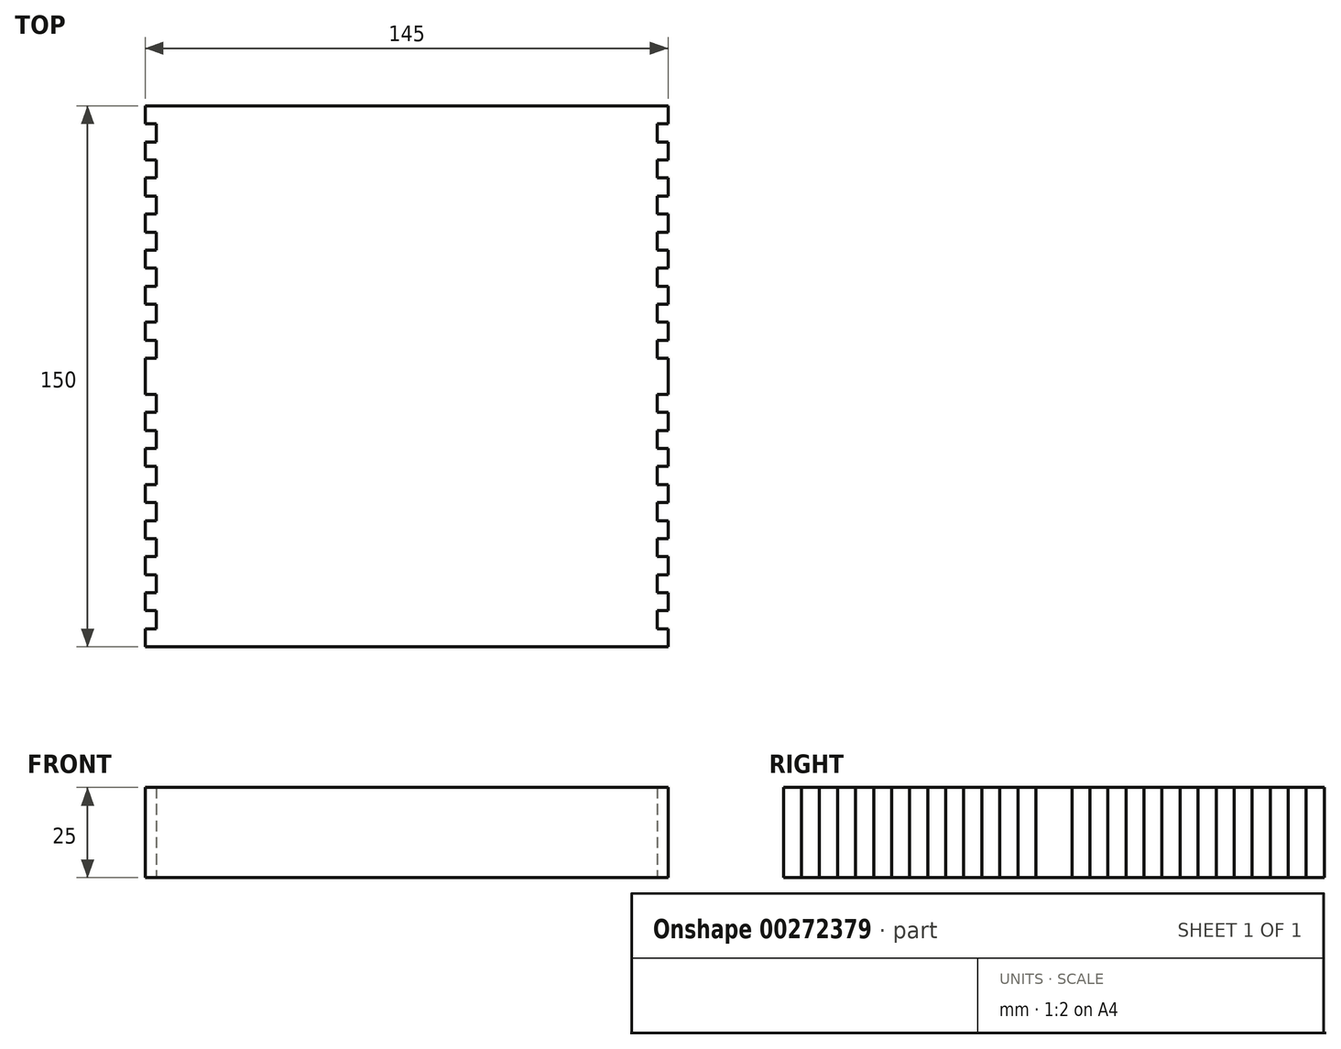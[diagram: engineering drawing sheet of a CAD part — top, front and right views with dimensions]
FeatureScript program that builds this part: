
annotation { "Feature Type Name" : "Feature", "Feature Type Description" : "" }
export const myFeature = defineFeature(function(context is Context, id is Id, definition is map)
    precondition{}
    {
        {
            var Q0;
            Q0=qCreatedBy(makeId("Top.planeOp"),FACE);
            var sketch = newSketch(context, id + "F0", { "sketchPlane" : qUnion([Q0])});
            skLineSegment(sketch, "E0.bottom", {"start": v(72.5, 75) * mm, "end": v(-72.5, 75) * mm});
            skLineSegment(sketch, "E0.top", {"start": v(72.5, -75) * mm, "end": v(-72.5, -75) * mm});
            skPoint(sketch, "E0.middle", {"position": v(0, 0) * mm});
            skLineSegment(sketch, "E1", {"start": v(-72.5, 0) * mm, "end": v(72.5, 0) * mm, "construction": true});
            skLineSegment(sketch, "E2", {"start": v(0, 75) * mm, "end": v(0, -75) * mm, "construction": true});
            skLineSegment(sketch, "E3", {"start": v(-72.5, 75) * mm, "end": v(-72.5, 70) * mm});
            skLineSegment(sketch, "E4", {"start": v(-72.5, 70) * mm, "end": v(-69.5, 70) * mm});
            skLineSegment(sketch, "E5", {"start": v(-69.5, 70) * mm, "end": v(-69.5, 65) * mm});
            skLineSegment(sketch, "E6", {"start": v(-69.5, 65) * mm, "end": v(-72.5, 65) * mm});
            skLineSegment(sketch, "E7", {"start": v(-72.5, 65) * mm, "end": v(-72.5, 60) * mm});
            skLineSegment(sketch, "E8", {"start": v(-72.5, 60) * mm, "end": v(-69.5, 60) * mm});
            skLineSegment(sketch, "E9", {"start": v(-69.5, 60) * mm, "end": v(-69.5, 55) * mm});
            skLineSegment(sketch, "E10", {"start": v(-69.5, 55) * mm, "end": v(-72.5, 55) * mm});
            skLineSegment(sketch, "E11", {"start": v(-72.5, 55) * mm, "end": v(-72.5, 50) * mm});
            skLineSegment(sketch, "E12", {"start": v(-72.5, 50) * mm, "end": v(-69.5, 50) * mm});
            skLineSegment(sketch, "E13", {"start": v(-69.5, 50) * mm, "end": v(-69.5, 45) * mm});
            skLineSegment(sketch, "E14", {"start": v(-69.5, 45) * mm, "end": v(-72.5, 45) * mm});
            skLineSegment(sketch, "E15", {"start": v(-72.5, 45) * mm, "end": v(-72.5, 40) * mm});
            skLineSegment(sketch, "E16", {"start": v(-72.5, 40) * mm, "end": v(-69.5, 40) * mm});
            skLineSegment(sketch, "E17", {"start": v(-69.5, 40) * mm, "end": v(-69.5, 35) * mm});
            skLineSegment(sketch, "E18", {"start": v(-69.5, 35) * mm, "end": v(-72.5, 35) * mm});
            skLineSegment(sketch, "E19", {"start": v(-72.5, 35) * mm, "end": v(-72.5, 30) * mm});
            skLineSegment(sketch, "E20", {"start": v(-72.5, 30) * mm, "end": v(-69.5, 30) * mm});
            skLineSegment(sketch, "E21", {"start": v(-69.5, 30) * mm, "end": v(-69.5, 25) * mm});
            skLineSegment(sketch, "E22", {"start": v(-69.5, 25) * mm, "end": v(-72.5, 25) * mm});
            skLineSegment(sketch, "E23", {"start": v(-72.5, 25) * mm, "end": v(-72.5, 20) * mm});
            skLineSegment(sketch, "E24", {"start": v(-72.5, 20) * mm, "end": v(-69.5, 20) * mm});
            skLineSegment(sketch, "E25", {"start": v(-69.5, 20) * mm, "end": v(-69.5, 15) * mm});
            skLineSegment(sketch, "E26", {"start": v(-69.5, 15) * mm, "end": v(-72.5, 15) * mm});
            skLineSegment(sketch, "E27", {"start": v(-72.5, 15) * mm, "end": v(-72.5, 10) * mm});
            skLineSegment(sketch, "E28", {"start": v(-72.5, 10) * mm, "end": v(-69.5, 10) * mm});
            skLineSegment(sketch, "E29", {"start": v(-69.5, 10) * mm, "end": v(-69.5, 5) * mm});
            skLineSegment(sketch, "E30", {"start": v(-69.5, 5) * mm, "end": v(-72.5, 5) * mm});
            skLineSegment(sketch, "E31", {"start": v(-72.5, 5) * mm, "end": v(-72.5, 0) * mm});
            skLineSegment(sketch, "E32.MirrorCS", {"start": v(-72.5, -75) * mm, "end": v(-72.5, -70) * mm});
            skLineSegment(sketch, "E33.MirrorCS", {"start": v(-69.5, -5) * mm, "end": v(-72.5, -5) * mm});
            skLineSegment(sketch, "E34.MirrorCS", {"start": v(-69.5, -45) * mm, "end": v(-72.5, -45) * mm});
            skLineSegment(sketch, "E35.MirrorCS", {"start": v(-72.5, -40) * mm, "end": v(-69.5, -40) * mm});
            skLineSegment(sketch, "E36.MirrorCS", {"start": v(-72.5, -15) * mm, "end": v(-72.5, -10) * mm});
            skLineSegment(sketch, "E37.MirrorCS", {"start": v(-72.5, -25) * mm, "end": v(-72.5, -20) * mm});
            skLineSegment(sketch, "E38.MirrorCS", {"start": v(-69.5, -55) * mm, "end": v(-72.5, -55) * mm});
            skLineSegment(sketch, "E39.MirrorCS", {"start": v(-69.5, -35) * mm, "end": v(-72.5, -35) * mm});
            skLineSegment(sketch, "E40.MirrorCS", {"start": v(-69.5, -60) * mm, "end": v(-69.5, -55) * mm});
            skLineSegment(sketch, "E41.MirrorCS", {"start": v(-72.5, -60) * mm, "end": v(-69.5, -60) * mm});
            skLineSegment(sketch, "E42.MirrorCS", {"start": v(-72.5, -5) * mm, "end": v(-72.5, 0) * mm});
            skLineSegment(sketch, "E43.MirrorCS", {"start": v(-72.5, -50) * mm, "end": v(-69.5, -50) * mm});
            skLineSegment(sketch, "E44.MirrorCS", {"start": v(-72.5, -30) * mm, "end": v(-69.5, -30) * mm});
            skLineSegment(sketch, "E45.MirrorCS", {"start": v(-72.5, -55) * mm, "end": v(-72.5, -50) * mm});
            skLineSegment(sketch, "E46.MirrorCS", {"start": v(-72.5, -45) * mm, "end": v(-72.5, -40) * mm});
            skLineSegment(sketch, "E47.MirrorCS", {"start": v(-69.5, -15) * mm, "end": v(-72.5, -15) * mm});
            skLineSegment(sketch, "E48.MirrorCS", {"start": v(-69.5, -65) * mm, "end": v(-72.5, -65) * mm});
            skLineSegment(sketch, "E49.MirrorCS", {"start": v(-69.5, -70) * mm, "end": v(-69.5, -65) * mm});
            skLineSegment(sketch, "E50.MirrorCS", {"start": v(-72.5, -10) * mm, "end": v(-69.5, -10) * mm});
            skLineSegment(sketch, "E51.MirrorCS", {"start": v(-72.5, -70) * mm, "end": v(-69.5, -70) * mm});
            skLineSegment(sketch, "E52.MirrorCS", {"start": v(-72.5, -20) * mm, "end": v(-69.5, -20) * mm});
            skLineSegment(sketch, "E53.MirrorCS", {"start": v(-72.5, -35) * mm, "end": v(-72.5, -30) * mm});
            skLineSegment(sketch, "E54.MirrorCS", {"start": v(-69.5, -25) * mm, "end": v(-72.5, -25) * mm});
            skLineSegment(sketch, "E55.MirrorCS", {"start": v(-69.5, -20) * mm, "end": v(-69.5, -15) * mm});
            skLineSegment(sketch, "E56.MirrorCS", {"start": v(-69.5, -50) * mm, "end": v(-69.5, -45) * mm});
            skLineSegment(sketch, "E57.MirrorCS", {"start": v(-69.5, -10) * mm, "end": v(-69.5, -5) * mm});
            skLineSegment(sketch, "E58.MirrorCS", {"start": v(-72.5, -65) * mm, "end": v(-72.5, -60) * mm});
            skLineSegment(sketch, "E59.MirrorCS", {"start": v(-69.5, -30) * mm, "end": v(-69.5, -25) * mm});
            skLineSegment(sketch, "E60.MirrorCS", {"start": v(-69.5, -40) * mm, "end": v(-69.5, -35) * mm});
            skLineSegment(sketch, "E61.MirrorCS", {"start": v(0, -75) * mm, "end": v(0, 75) * mm, "construction": true});
            skLineSegment(sketch, "E62.MirrorCS", {"start": v(72.5, 75) * mm, "end": v(72.5, 70) * mm});
            skLineSegment(sketch, "E63.MirrorCS", {"start": v(72.5, -75) * mm, "end": v(72.5, -70) * mm});
            skLineSegment(sketch, "E64.MirrorCS", {"start": v(69.5, -20) * mm, "end": v(69.5, -15) * mm});
            skLineSegment(sketch, "E65.MirrorCS", {"start": v(69.5, 25) * mm, "end": v(72.5, 25) * mm});
            skLineSegment(sketch, "E66.MirrorCS", {"start": v(69.5, -25) * mm, "end": v(72.5, -25) * mm});
            skLineSegment(sketch, "E67.MirrorCS", {"start": v(69.5, -65) * mm, "end": v(72.5, -65) * mm});
            skLineSegment(sketch, "E68.MirrorCS", {"start": v(69.5, 55) * mm, "end": v(72.5, 55) * mm});
            skLineSegment(sketch, "E69.MirrorCS", {"start": v(72.5, 60) * mm, "end": v(69.5, 60) * mm});
            skLineSegment(sketch, "E70.MirrorCS", {"start": v(72.5, 65) * mm, "end": v(72.5, 60) * mm});
            skLineSegment(sketch, "E71.MirrorCS", {"start": v(72.5, 50) * mm, "end": v(69.5, 50) * mm});
            skLineSegment(sketch, "E72.MirrorCS", {"start": v(72.5, 55) * mm, "end": v(72.5, 50) * mm});
            skLineSegment(sketch, "E73.MirrorCS", {"start": v(69.5, -15) * mm, "end": v(72.5, -15) * mm});
            skLineSegment(sketch, "E74.MirrorCS", {"start": v(69.5, -40) * mm, "end": v(69.5, -35) * mm});
            skLineSegment(sketch, "E75.MirrorCS", {"start": v(69.5, -55) * mm, "end": v(72.5, -55) * mm});
            skLineSegment(sketch, "E76.MirrorCS", {"start": v(69.5, 45) * mm, "end": v(72.5, 45) * mm});
            skLineSegment(sketch, "E77.MirrorCS", {"start": v(72.5, 70) * mm, "end": v(69.5, 70) * mm});
            skLineSegment(sketch, "E78.MirrorCS", {"start": v(69.5, 30) * mm, "end": v(69.5, 25) * mm});
            skLineSegment(sketch, "E79.MirrorCS", {"start": v(69.5, -45) * mm, "end": v(72.5, -45) * mm});
            skLineSegment(sketch, "E80.MirrorCS", {"start": v(72.5, -10) * mm, "end": v(69.5, -10) * mm});
            skLineSegment(sketch, "E81.MirrorCS", {"start": v(72.5, -20) * mm, "end": v(69.5, -20) * mm});
            skLineSegment(sketch, "E82.MirrorCS", {"start": v(72.5, -65) * mm, "end": v(72.5, -60) * mm});
            skLineSegment(sketch, "E83.MirrorCS", {"start": v(72.5, -50) * mm, "end": v(69.5, -50) * mm});
            skLineSegment(sketch, "E84.MirrorCS", {"start": v(69.5, 65) * mm, "end": v(72.5, 65) * mm});
            skLineSegment(sketch, "E85.MirrorCS", {"start": v(69.5, -10) * mm, "end": v(69.5, -5) * mm});
            skLineSegment(sketch, "E86.MirrorCS", {"start": v(69.5, 35) * mm, "end": v(72.5, 35) * mm});
            skLineSegment(sketch, "E87.MirrorCS", {"start": v(72.5, 45) * mm, "end": v(72.5, 40) * mm});
            skLineSegment(sketch, "E88.MirrorCS", {"start": v(72.5, -60) * mm, "end": v(69.5, -60) * mm});
            skLineSegment(sketch, "E89.MirrorCS", {"start": v(69.5, 20) * mm, "end": v(69.5, 15) * mm});
            skLineSegment(sketch, "E90.MirrorCS", {"start": v(72.5, 30) * mm, "end": v(69.5, 30) * mm});
            skLineSegment(sketch, "E91.MirrorCS", {"start": v(69.5, 10) * mm, "end": v(69.5, 5) * mm});
            skLineSegment(sketch, "E92.MirrorCS", {"start": v(69.5, -5) * mm, "end": v(72.5, -5) * mm});
            skLineSegment(sketch, "E93.MirrorCS", {"start": v(72.5, 10) * mm, "end": v(69.5, 10) * mm});
            skLineSegment(sketch, "E94.MirrorCS", {"start": v(72.5, -30) * mm, "end": v(69.5, -30) * mm});
            skLineSegment(sketch, "E95.MirrorCS", {"start": v(72.5, 40) * mm, "end": v(69.5, 40) * mm});
            skLineSegment(sketch, "E96.MirrorCS", {"start": v(72.5, 20) * mm, "end": v(69.5, 20) * mm});
            skLineSegment(sketch, "E97.MirrorCS", {"start": v(69.5, -35) * mm, "end": v(72.5, -35) * mm});
            skLineSegment(sketch, "E98.MirrorCS", {"start": v(69.5, 15) * mm, "end": v(72.5, 15) * mm});
            skLineSegment(sketch, "E99.MirrorCS", {"start": v(69.5, 5) * mm, "end": v(72.5, 5) * mm});
            skLineSegment(sketch, "E100.MirrorCS", {"start": v(72.5, -70) * mm, "end": v(69.5, -70) * mm});
            skLineSegment(sketch, "E101.MirrorCS", {"start": v(69.5, -50) * mm, "end": v(69.5, -45) * mm});
            skLineSegment(sketch, "E102.MirrorCS", {"start": v(72.5, -5) * mm, "end": v(72.5, 0) * mm});
            skLineSegment(sketch, "E103.MirrorCS", {"start": v(69.5, -30) * mm, "end": v(69.5, -25) * mm});
            skLineSegment(sketch, "E104.MirrorCS", {"start": v(72.5, -55) * mm, "end": v(72.5, -50) * mm});
            skLineSegment(sketch, "E105.MirrorCS", {"start": v(72.5, -40) * mm, "end": v(69.5, -40) * mm});
            skLineSegment(sketch, "E106.MirrorCS", {"start": v(69.5, 40) * mm, "end": v(69.5, 35) * mm});
            skLineSegment(sketch, "E107.MirrorCS", {"start": v(72.5, 15) * mm, "end": v(72.5, 10) * mm});
            skLineSegment(sketch, "E108.MirrorCS", {"start": v(69.5, 50) * mm, "end": v(69.5, 45) * mm});
            skLineSegment(sketch, "E109.MirrorCS", {"start": v(72.5, -45) * mm, "end": v(72.5, -40) * mm});
            skLineSegment(sketch, "E110.MirrorCS", {"start": v(72.5, 25) * mm, "end": v(72.5, 20) * mm});
            skLineSegment(sketch, "E111.MirrorCS", {"start": v(72.5, -25) * mm, "end": v(72.5, -20) * mm});
            skLineSegment(sketch, "E112.MirrorCS", {"start": v(72.5, -35) * mm, "end": v(72.5, -30) * mm});
            skLineSegment(sketch, "E113.MirrorCS", {"start": v(72.5, 5) * mm, "end": v(72.5, 0) * mm});
            skLineSegment(sketch, "E114.MirrorCS", {"start": v(69.5, 60) * mm, "end": v(69.5, 55) * mm});
            skLineSegment(sketch, "E115.MirrorCS", {"start": v(69.5, 70) * mm, "end": v(69.5, 65) * mm});
            skLineSegment(sketch, "E116.MirrorCS", {"start": v(72.5, -15) * mm, "end": v(72.5, -10) * mm});
            skLineSegment(sketch, "E117.MirrorCS", {"start": v(69.5, -70) * mm, "end": v(69.5, -65) * mm});
            skLineSegment(sketch, "E118.MirrorCS", {"start": v(69.5, -60) * mm, "end": v(69.5, -55) * mm});
            skLineSegment(sketch, "E119.MirrorCS", {"start": v(72.5, 35) * mm, "end": v(72.5, 30) * mm});
            skSolve(sketch);
        }
        {
            var Q0;
            Q0=makeQuery(id+"F0.imprint","IMPRINT",FACE,{"disambiguationData":[TD([[makeQuery(id+"F0.imprint","IMPRINT",EDGE,{"derivedFrom":sQuery(id+"F0.wireOp",EDGE,"E0.bottom")}),1.0]])]});
            extrude(context, id + "F1", {"entities" : qUnion([Q0]), "depth" : 25 * mm});
        }
    });
